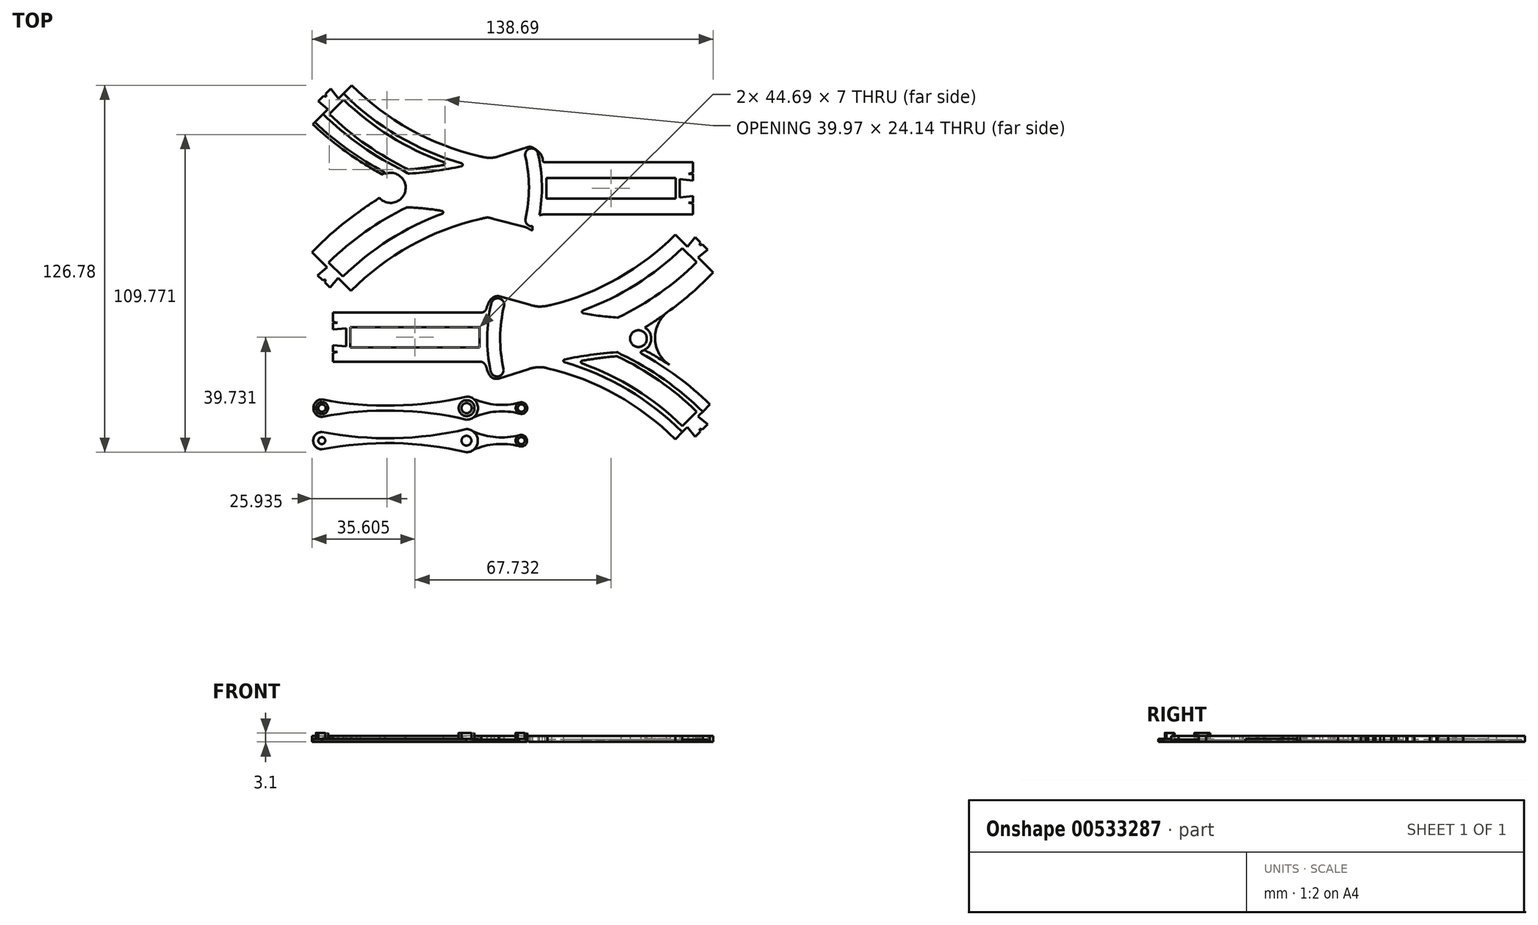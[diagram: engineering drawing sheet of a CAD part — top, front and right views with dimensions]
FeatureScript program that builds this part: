
annotation { "Feature Type Name" : "Feature", "Feature Type Description" : "" }
export const myFeature = defineFeature(function(context is Context, id is Id, definition is map)
    precondition{}
    {
        {
            var Q0;
            Q0=qCreatedBy(makeId("Top.planeOp"),FACE);
            var sketch = newSketch(context, id + "F0", { "sketchPlane" : qUnion([Q0])});
            skLineSegment(sketch, "E0.right", {"start": v(-61.89, -40.1) * mm, "end": v(-61.89, -35.5) * mm});
            skLineSegment(sketch, "E1.bottom", {"start": v(-10.59, -38.6) * mm, "end": v(-61.89, -38.6) * mm});
            skLineSegment(sketch, "E1.right", {"start": v(-61.89, -38.6) * mm, "end": v(-61.89, -40.1) * mm});
            skLineSegment(sketch, "E2.top", {"start": v(-10.59, -21.6) * mm, "end": v(-61.89, -21.6) * mm});
            skLineSegment(sketch, "E2.right", {"start": v(-61.89, -20.1) * mm, "end": v(-61.89, -21.6) * mm});
            skLineSegment(sketch, "E3.top", {"start": v(-10.32, -35.1) * mm, "end": v(-61.89, -35.1) * mm});
            skLineSegment(sketch, "E3.right", {"start": v(-61.89, -38.6) * mm, "end": v(-61.89, -35.5) * mm});
            skLineSegment(sketch, "E4.top", {"start": v(-10.32, -25.1) * mm, "end": v(-61.89, -25.1) * mm});
            skLineSegment(sketch, "E4.right", {"start": v(-61.89, -21.6) * mm, "end": v(-61.89, -24.7) * mm});
            skLineSegment(sketch, "E5", {"start": v(-57.4, -33.26) * mm, "end": v(-61.89, -32.8) * mm});
            skLineSegment(sketch, "E6.MirrorCS", {"start": v(-57.4, -26.96) * mm, "end": v(-61.89, -27.4) * mm});
            skLineSegment(sketch, "E7", {"start": v(-57.4, -33.26) * mm, "end": v(-57.4, -26.96) * mm});
            skLineSegment(sketch, "E8.trimOffspring", {"start": v(-61.89, -24.7) * mm, "end": v(-61.89, -20.1) * mm});
            skLineSegment(sketch, "E9", {"start": v(-61.89, -35.1) * mm, "end": v(-61.89, -32.8) * mm});
            skLineSegment(sketch, "E10", {"start": v(-61.89, -27.4) * mm, "end": v(-61.89, -25.1) * mm});
            skLineSegment(sketch, "E11", {"start": v(-61.89, -35.5) * mm, "end": v(-60.39, -35.1) * mm});
            skLineSegment(sketch, "E12", {"start": v(-61.89, -24.7) * mm, "end": v(-60.39, -25.1) * mm});
            skLineSegment(sketch, "E13.right", {"start": v(-55.9, -33.6) * mm, "end": v(-55.9, -30.1) * mm});
            skArc(sketch, "E14", {"start": v(13.02, -17.5) * mm, "mid": v(35.83, -8.48) * mm, "end": v(55.36, 6.37) * mm});
            skArc(sketch, "E15", {"start": v(13.65, -18.9) * mm, "mid": v(36.7, -9.71) * mm, "end": v(56.42, 5.31) * mm});
            skArc(sketch, "E16", {"start": v(18.9, -21.08) * mm, "mid": v(40.39, -11.61) * mm, "end": v(58.9, 2.84) * mm});
            skArc(sketch, "E17", {"start": v(24.51, -20.8) * mm, "mid": v(42.85, -11.86) * mm, "end": v(58.9, 0.73) * mm});
            skArc(sketch, "E18", {"start": v(37.87, -24.35) * mm, "mid": v(52.76, -15.45) * mm, "end": v(65.98, -4.22) * mm});
            skArc(sketch, "E19", {"start": v(11.95, -42.28) * mm, "mid": v(35.32, -51.31) * mm, "end": v(55.33, -66.4) * mm});
            skArc(sketch, "E20", {"start": v(12.09, -40.78) * mm, "mid": v(35.96, -49.95) * mm, "end": v(56.39, -65.34) * mm});
            skArc(sketch, "E21", {"start": v(18.13, -38.74) * mm, "mid": v(40.02, -48.24) * mm, "end": v(58.86, -62.87) * mm});
            skLineSegment(sketch, "E22", {"start": v(55.36, 6.37) * mm, "end": v(60.58, 1.17) * mm});
            skLineSegment(sketch, "E23", {"start": v(55.33, -66.4) * mm, "end": v(59.92, -61.8) * mm});
            skArc(sketch, "E24.trimOffspring", {"start": v(24.17, -39.14) * mm, "mid": v(42.67, -48.1) * mm, "end": v(58.85, -60.75) * mm});
            skArc(sketch, "E25.trimOffspring", {"start": v(36.3, -36.62) * mm, "mid": v(50.84, -45.1) * mm, "end": v(63.8, -55.8) * mm});
            skArc(sketch, "E26.trimOffspring", {"start": v(37.7, -36) * mm, "mid": v(52.64, -44.73) * mm, "end": v(65.93, -55.8) * mm});
            skArc(sketch, "E27.trimOffspring", {"start": v(44.78, -35.76) * mm, "mid": v(57.2, -43.74) * mm, "end": v(68.4, -53.32) * mm});
            skArc(sketch, "E28.trimOffspring", {"start": v(36.76, -23.23) * mm, "mid": v(51.07, -14.81) * mm, "end": v(63.85, -4.22) * mm});
            skArc(sketch, "E29", {"start": v(54.66, -20.73) * mm, "mid": v(62.38, -14.58) * mm, "end": v(69.52, -7.75) * mm});
            skArc(sketch, "E30", {"start": v(54.4, -39.65) * mm, "mid": v(62.22, -45.62) * mm, "end": v(69.47, -52.26) * mm});
            skArc(sketch, "E31", {"start": v(54.66, -20.73) * mm, "mid": v(49.42, -30.12) * mm, "end": v(54.4, -39.65) * mm});
            skArc(sketch, "E32", {"start": v(-4.25, -15.97) * mm, "mid": v(-5.74, -15.98) * mm, "end": v(-7.04, -16.7) * mm});
            skCircle(sketch, "E33", {"center": v(43.7, -30.57) * mm, "radius": 2.9 * mm});
            skArc(sketch, "E34", {"start": v(-2.75, -19.24) * mm, "mid": v(-4.58, -16.66) * mm, "end": v(-7.18, -18.46) * mm});
            skArc(sketch, "E35.trimOffspring", {"start": v(44.57, -25.78) * mm, "mid": v(57.19, -17.08) * mm, "end": v(68.46, -6.7) * mm});
            skArc(sketch, "E36.trimOffspring", {"start": v(45.91, -26.73) * mm, "mid": v(50.36, -23.84) * mm, "end": v(54.66, -20.73) * mm});
            skArc(sketch, "E37.trimOffspring", {"start": v(45.73, -34.5) * mm, "mid": v(50.13, -36.98) * mm, "end": v(54.4, -39.65) * mm});
            skLineSegment(sketch, "E38", {"start": v(-55.9, -26.6) * mm, "end": v(-11.22, -26.6) * mm});
            skLineSegment(sketch, "E39", {"start": v(-55.9, -33.6) * mm, "end": v(-11.22, -33.6) * mm});
            skArc(sketch, "E40", {"start": v(36.17, -35.27) * mm, "mid": v(27.12, -36.2) * mm, "end": v(18.17, -37.77) * mm});
            skLineSegment(sketch, "E41", {"start": v(18.9, -21.08) * mm, "end": v(18.39, -21.24) * mm});
            skLineSegment(sketch, "E42", {"start": v(37.87, -24.35) * mm, "end": v(37.02, -24.88) * mm});
            skLineSegment(sketch, "E43", {"start": v(12.09, -40.78) * mm, "end": v(11.44, -40.63) * mm});
            skLineSegment(sketch, "E44", {"start": v(37.7, -36) * mm, "end": v(36.76, -35.42) * mm});
            skLineSegment(sketch, "E45", {"start": v(6.23, -18.9) * mm, "end": v(-4.25, -15.97) * mm});
            skFitSpline(sketch, "E46", {"points": [v(-8.82, -20.06) * mm, v(-7.04, -16.7) * mm, v(-4.25, -15.97) * mm], "startDerivative": vector(2.43, 8.58) * mm, "endDerivative": vector(7.45, -1.74) * mm});
            skLineSegment(sketch, "E47", {"start": v(5.76, -41.06) * mm, "end": v(-4.6, -44.37) * mm});
            skFitSpline(sketch, "E48", {"points": [v(-8.98, -40.2) * mm, v(-7.4, -43.67) * mm, v(-4.6, -44.37) * mm], "startDerivative": vector(2.7, -8.06) * mm, "endDerivative": vector(7.78, 1.84) * mm});
            skArc(sketch, "E49", {"start": v(-7.13, -18.25) * mm, "mid": v(-8.6, -30.15) * mm, "end": v(-7.32, -42.07) * mm});
            skArc(sketch, "E50", {"start": v(-2.75, -19.24) * mm, "mid": v(-4.11, -30.11) * mm, "end": v(-2.96, -41.01) * mm});
            skArc(sketch, "E51", {"start": v(-7.4, -41.72) * mm, "mid": v(-4.82, -43.63) * mm, "end": v(-2.96, -41.01) * mm});
            skLineSegment(sketch, "E52", {"start": v(-4.02, -45.87) * mm, "end": v(6.3, -42.46) * mm});
            skLineSegment(sketch, "E53", {"start": v(14.4, -19.56) * mm, "end": v(14.4, -19.56) * mm});
            skFitSpline(sketch, "E54", {"points": [v(-4.02, -45.87) * mm, v(-8.28, -44.88) * mm, v(-10.33, -40.85) * mm], "startDerivative": vector(-10.27, -1.82) * mm, "endDerivative": vector(-1.73, 10.08) * mm});
            skLineSegment(sketch, "E55", {"start": v(6.35, -17.37) * mm, "end": v(-4.44, -14.36) * mm});
            skFitSpline(sketch, "E56", {"points": [v(6.3, -42.46) * mm, v(11.95, -42.28) * mm], "startDerivative": vector(4.48, 1.48) * mm, "endDerivative": vector(4.94, -1) * mm});
            skFitSpline(sketch, "E57", {"points": [v(5.76, -41.06) * mm, v(12.29, -40.82) * mm], "startDerivative": vector(6.34, 1.97) * mm, "endDerivative": vector(7.02, -1.91) * mm});
            skArc(sketch, "E58.trimOffspring", {"start": v(18.42, -22.2) * mm, "mid": v(27.52, -23.9) * mm, "end": v(36.71, -24.95) * mm});
            skFitSpline(sketch, "E59", {"points": [v(-4.44, -14.36) * mm, v(-7.95, -15.52) * mm, v(-10.15, -19.36) * mm], "startDerivative": vector(-8.7, -0.53) * mm, "endDerivative": vector(-3.43, -9.13) * mm});
            skFitSpline(sketch, "E60", {"points": [v(6.35, -17.37) * mm, v(13.02, -17.5) * mm], "startDerivative": vector(8.86, -2.5) * mm, "endDerivative": vector(9.69, 2.19) * mm});
            skFitSpline(sketch, "E61", {"points": [v(6.23, -18.9) * mm, v(13.65, -18.9) * mm], "startDerivative": vector(7.97, -2.48) * mm, "endDerivative": vector(9.92, 2.27) * mm});
            skFitSpline(sketch, "E62", {"points": [v(-14.72, -20.1) * mm, v(-8.7, -16.34) * mm], "startDerivative": vector(9.37, 0) * mm, "endDerivative": vector(3.18, 5.82) * mm});
            skLineSegment(sketch, "E63.trimOffspring", {"start": v(-14.72, -20.1) * mm, "end": v(-61.89, -20.1) * mm});
            skFitSpline(sketch, "E64", {"points": [v(-10.59, -21.6) * mm, v(-8.82, -20.06) * mm], "startDerivative": vector(2.32, 0.32) * mm, "endDerivative": vector(0.74, 2.93) * mm});
            skArc(sketch, "E65.trimOffspring", {"start": v(-9.58, -25.91) * mm, "mid": v(-9.72, -30.1) * mm, "end": v(-9.58, -34.3) * mm});
            skArc(sketch, "E66.filletArc", {"start": v(-9.58, -25.91) * mm, "mid": v(-9.78, -25.35) * mm, "end": v(-10.32, -25.1) * mm});
            skArc(sketch, "E67.filletArc", {"start": v(-10.32, -35.1) * mm, "mid": v(-9.78, -34.87) * mm, "end": v(-9.58, -34.3) * mm});
            skFitSpline(sketch, "E68", {"points": [v(-14.72, -40.1) * mm, v(-9.07, -44.04) * mm], "startDerivative": vector(9.23, 0) * mm, "endDerivative": vector(3.36, -5.87) * mm});
            skLineSegment(sketch, "E69.trimOffspring", {"start": v(-14.72, -40.1) * mm, "end": v(-61.89, -40.1) * mm});
            skFitSpline(sketch, "E70", {"points": [v(-10.59, -38.6) * mm, v(-8.98, -40.2) * mm], "startDerivative": vector(2.4, -0.42) * mm, "endDerivative": vector(0.75, -2.2) * mm});
            skArc(sketch, "E71", {"start": v(44.89, -34.84) * mm, "mid": v(48.13, -30.44) * mm, "end": v(44.64, -26.24) * mm});
            skLineSegment(sketch, "E72", {"start": v(-11.22, -26.6) * mm, "end": v(-11.22, -33.6) * mm});
            skFitSpline(sketch, "E73", {"points": [v(22.86, -21.39) * mm, v(36.65, -23.28) * mm], "startDerivative": vector(10.75, -2.48) * mm, "endDerivative": vector(16.26, -0.75) * mm});
            skArc(sketch, "E74.filletArc", {"start": v(24.51, -20.8) * mm, "mid": v(24.19, -21.31) * mm, "end": v(24.58, -21.76) * mm});
            skArc(sketch, "E75.filletArc", {"start": v(36.52, -23.28) * mm, "mid": v(36.64, -23.27) * mm, "end": v(36.76, -23.23) * mm});
            skFitSpline(sketch, "E76", {"points": [v(22.35, -38.51) * mm, v(36.3, -36.62) * mm], "startDerivative": vector(13.99, 2.55) * mm, "endDerivative": vector(14.95, 1.52) * mm});
            skArc(sketch, "E77.filletArc", {"start": v(24.26, -38.18) * mm, "mid": v(23.84, -38.63) * mm, "end": v(24.17, -39.14) * mm});
            skLineSegment(sketch, "E78", {"start": v(64.85, 1.72) * mm, "end": v(65.81, 1.98) * mm});
            skLineSegment(sketch, "E79", {"start": v(65.81, 1.98) * mm, "end": v(67.6, 0.2) * mm});
            skLineSegment(sketch, "E80", {"start": v(67.6, 0.2) * mm, "end": v(64.3, -2.55) * mm});
            skLineSegment(sketch, "E81.MirrorCS", {"start": v(63.28, 4.5) * mm, "end": v(60.58, 1.17) * mm});
            skLineSegment(sketch, "E82.MirrorCS", {"start": v(65.1, 2.69) * mm, "end": v(63.28, 4.5) * mm});
            skLineSegment(sketch, "E83.MirrorCS", {"start": v(64.85, 1.72) * mm, "end": v(65.1, 2.69) * mm});
            skLineSegment(sketch, "E84", {"start": v(64.84, -61.73) * mm, "end": v(65.1, -62.7) * mm});
            skLineSegment(sketch, "E85", {"start": v(65.1, -62.7) * mm, "end": v(63.3, -64.5) * mm});
            skLineSegment(sketch, "E86", {"start": v(63.3, -64.5) * mm, "end": v(60.59, -61.16) * mm});
            skLineSegment(sketch, "E87.MirrorCS", {"start": v(67.6, -60.18) * mm, "end": v(64.26, -57.48) * mm});
            skLineSegment(sketch, "E88.MirrorCS", {"start": v(65.8, -61.99) * mm, "end": v(67.6, -60.18) * mm});
            skLineSegment(sketch, "E89.MirrorCS", {"start": v(64.84, -61.73) * mm, "end": v(65.8, -61.99) * mm});
            skArc(sketch, "E90.filletArc", {"start": v(18.17, -37.77) * mm, "mid": v(17.77, -38.24) * mm, "end": v(18.13, -38.74) * mm});
            skPoint(sketch, "E91.visualSharp", {"position": v(36.5, -35.25) * mm});
            skArc(sketch, "E91.filletArc", {"start": v(36.76, -35.42) * mm, "mid": v(36.48, -35.3) * mm, "end": v(36.17, -35.27) * mm});
            skPoint(sketch, "E92.visualSharp", {"position": v(43.36, -35) * mm});
            skArc(sketch, "E92.filletArc", {"start": v(44.89, -34.84) * mm, "mid": v(44.53, -35.26) * mm, "end": v(44.78, -35.76) * mm});
            skPoint(sketch, "E93.visualSharp", {"position": v(16.57, -21.78) * mm});
            skArc(sketch, "E93.filletArc", {"start": v(18.39, -21.24) * mm, "mid": v(18.03, -21.74) * mm, "end": v(18.42, -22.2) * mm});
            skPoint(sketch, "E94.visualSharp", {"position": v(36.88, -24.96) * mm});
            skArc(sketch, "E94.filletArc", {"start": v(36.71, -24.95) * mm, "mid": v(36.87, -24.94) * mm, "end": v(37.02, -24.88) * mm});
            skPoint(sketch, "E95.visualSharp", {"position": v(43.95, -26.14) * mm});
            skArc(sketch, "E95.filletArc", {"start": v(44.57, -25.78) * mm, "mid": v(44.45, -26.03) * mm, "end": v(44.64, -26.24) * mm});
            skLineSegment(sketch, "E96", {"start": v(-55.9, -30.1) * mm, "end": v(-55.9, -26.6) * mm});
            skLineSegment(sketch, "E97.trimOffspring", {"start": v(64.3, -2.55) * mm, "end": v(69.52, -7.75) * mm});
            skLineSegment(sketch, "E98.trimOffspring", {"start": v(64.87, -56.86) * mm, "end": v(69.47, -52.26) * mm});
            skLineSegment(sketch, "E99", {"start": v(60.59, -61.16) * mm, "end": v(59.92, -61.8) * mm});
            skLineSegment(sketch, "E100", {"start": v(64.26, -57.48) * mm, "end": v(64.87, -56.86) * mm});
            skLineSegment(sketch, "E101.right", {"start": v(62.49, 31.38) * mm, "end": v(62.49, 26.78) * mm});
            skLineSegment(sketch, "E102.bottom", {"start": v(11.19, 30.38) * mm, "end": v(62.49, 30.38) * mm});
            skLineSegment(sketch, "E102.right", {"start": v(62.49, 30.38) * mm, "end": v(62.49, 31.38) * mm});
            skLineSegment(sketch, "E103.top", {"start": v(11.19, 12.38) * mm, "end": v(62.49, 12.38) * mm});
            skLineSegment(sketch, "E103.right", {"start": v(62.49, 11.38) * mm, "end": v(62.49, 12.38) * mm});
            skLineSegment(sketch, "E104.top", {"start": v(10.92, 26.38) * mm, "end": v(62.49, 26.38) * mm});
            skLineSegment(sketch, "E104.right", {"start": v(62.49, 30.38) * mm, "end": v(62.49, 26.78) * mm});
            skLineSegment(sketch, "E105.top", {"start": v(10.92, 16.38) * mm, "end": v(62.49, 16.38) * mm});
            skLineSegment(sketch, "E105.right", {"start": v(62.49, 12.38) * mm, "end": v(62.49, 15.98) * mm});
            skLineSegment(sketch, "E106", {"start": v(58, 24.53) * mm, "end": v(62.49, 24.08) * mm});
            skLineSegment(sketch, "E107.MirrorCS", {"start": v(58, 18.23) * mm, "end": v(62.49, 18.68) * mm});
            skLineSegment(sketch, "E108", {"start": v(58, 24.53) * mm, "end": v(58, 18.23) * mm});
            skLineSegment(sketch, "E109.trimOffspring", {"start": v(62.49, 15.98) * mm, "end": v(62.49, 11.38) * mm});
            skLineSegment(sketch, "E110", {"start": v(62.49, 26.38) * mm, "end": v(62.49, 24.08) * mm});
            skLineSegment(sketch, "E111", {"start": v(62.49, 18.68) * mm, "end": v(62.49, 16.38) * mm});
            skLineSegment(sketch, "E112", {"start": v(62.49, 26.78) * mm, "end": v(60.99, 26.38) * mm});
            skLineSegment(sketch, "E113", {"start": v(62.49, 15.98) * mm, "end": v(60.99, 16.38) * mm});
            skLineSegment(sketch, "E114.right", {"start": v(56.5, 24.88) * mm, "end": v(56.5, 21.38) * mm});
            skArc(sketch, "E115", {"start": v(-12.42, 9.41) * mm, "mid": v(-35.35, 0.23) * mm, "end": v(-54.94, -14.8) * mm});
            skArc(sketch, "E116", {"start": v(-11.23, 10.72) * mm, "mid": v(-35.2, 1.46) * mm, "end": v(-55.65, -14.1) * mm});
            skArc(sketch, "E117", {"start": v(-18.02, 13.06) * mm, "mid": v(-39.79, 3.43) * mm, "end": v(-58.5, -11.29) * mm});
            skArc(sketch, "E118", {"start": v(-24.13, 12.6) * mm, "mid": v(-42.47, 3.53) * mm, "end": v(-58.5, -9.17) * mm});
            skArc(sketch, "E119", {"start": v(-37.5, 16.08) * mm, "mid": v(-52.4, 7.08) * mm, "end": v(-65.61, -4.25) * mm});
            skArc(sketch, "E120", {"start": v(-11.36, 33.53) * mm, "mid": v(-34.74, 42.56) * mm, "end": v(-54.74, 57.65) * mm});
            skArc(sketch, "E121", {"start": v(-11.38, 32.5) * mm, "mid": v(-35.13, 41.63) * mm, "end": v(-55.45, 56.94) * mm});
            skArc(sketch, "E122", {"start": v(-17.42, 29.95) * mm, "mid": v(-39.38, 39.45) * mm, "end": v(-58.28, 54.11) * mm});
            skLineSegment(sketch, "E123", {"start": v(-54.94, -14.8) * mm, "end": v(-60.18, -9.62) * mm});
            skLineSegment(sketch, "E124", {"start": v(-54.74, 57.65) * mm, "end": v(-59.34, 53.05) * mm});
            skArc(sketch, "E125.trimOffspring", {"start": v(-23.58, 30.4) * mm, "mid": v(-42.08, 39.34) * mm, "end": v(-58.27, 52) * mm});
            skArc(sketch, "E126.trimOffspring", {"start": v(-35.7, 27.86) * mm, "mid": v(-50.25, 36.33) * mm, "end": v(-63.22, 47.05) * mm});
            skArc(sketch, "E127.trimOffspring", {"start": v(-37.13, 27.23) * mm, "mid": v(-52.06, 35.97) * mm, "end": v(-65.35, 47.04) * mm});
            skArc(sketch, "E128.trimOffspring", {"start": v(-44.1, 26.9) * mm, "mid": v(-56.74, 34.73) * mm, "end": v(-68.18, 44.21) * mm});
            skArc(sketch, "E129.trimOffspring", {"start": v(-36.43, 14.75) * mm, "mid": v(-50.72, 6.34) * mm, "end": v(-63.48, -4.25) * mm});
            skArc(sketch, "E130", {"start": v(-53.82, 12.6) * mm, "mid": v(-61.8, 6.28) * mm, "end": v(-69.17, -0.74) * mm});
            skArc(sketch, "E131", {"start": v(-53.57, 31.35) * mm, "mid": v(-61.5, 37.09) * mm, "end": v(-68.89, 43.5) * mm});
            skArc(sketch, "E132", {"start": v(-53.82, 12.6) * mm, "mid": v(-48.6, 21.9) * mm, "end": v(-53.57, 31.35) * mm});
            skArc(sketch, "E133", {"start": v(4.32, 8.02) * mm, "mid": v(5.36, 7.29) * mm, "end": v(6.59, 6.96) * mm});
            skCircle(sketch, "E134", {"center": v(-41.99, 21.52) * mm, "radius": 2.9 * mm});
            skArc(sketch, "E135", {"start": v(4.62, 10.76) * mm, "mid": v(6.6, 8.23) * mm, "end": v(9.1, 10.28) * mm});
            skArc(sketch, "E136.trimOffspring", {"start": v(-44.8, 17.5) * mm, "mid": v(-57.3, 8.86) * mm, "end": v(-68.45, -1.45) * mm});
            skArc(sketch, "E137.trimOffspring", {"start": v(-45.43, 18.29) * mm, "mid": v(-49.7, 15.54) * mm, "end": v(-53.82, 12.6) * mm});
            skArc(sketch, "E138.trimOffspring", {"start": v(-44.63, 26.05) * mm, "mid": v(-49.16, 28.6) * mm, "end": v(-53.57, 31.35) * mm});
            skLineSegment(sketch, "E139", {"start": v(56.5, 17.88) * mm, "end": v(11.82, 17.88) * mm});
            skLineSegment(sketch, "E140", {"start": v(56.5, 24.88) * mm, "end": v(11.82, 24.88) * mm});
            skArc(sketch, "E141", {"start": v(-35.51, 26.46) * mm, "mid": v(-26.44, 27.4) * mm, "end": v(-17.46, 28.98) * mm});
            skLineSegment(sketch, "E142", {"start": v(-18.02, 13.06) * mm, "end": v(-18.02, 13.06) * mm});
            skLineSegment(sketch, "E143", {"start": v(-37.5, 16.08) * mm, "end": v(-36.53, 16.67) * mm});
            skLineSegment(sketch, "E144", {"start": v(-11.58, 32.55) * mm, "end": v(-11.38, 32.5) * mm});
            skLineSegment(sketch, "E145", {"start": v(-37.13, 27.23) * mm, "end": v(-36.12, 26.61) * mm});
            skLineSegment(sketch, "E146", {"start": v(-6.22, 10.72) * mm, "end": v(4.32, 8.02) * mm});
            skFitSpline(sketch, "E147", {"points": [v(6.94, 10.75) * mm, v(7, 6.96) * mm, v(4.32, 8.02) * mm], "startDerivative": vector(-1.82, -6.41) * mm, "endDerivative": vector(-8.94, 2.16) * mm});
            skLineSegment(sketch, "E148", {"start": v(-5.03, 32.29) * mm, "end": v(5.33, 35.59) * mm});
            skFitSpline(sketch, "E149", {"points": [v(10.52, 31.9) * mm, v(8.12, 34.84) * mm, v(5.33, 35.59) * mm], "startDerivative": vector(-2.67, 7.98) * mm, "endDerivative": vector(-7.78, -1.84) * mm});
            skArc(sketch, "E150", {"start": v(8.96, 9.68) * mm, "mid": v(10.31, 21.68) * mm, "end": v(8.88, 33.66) * mm});
            skArc(sketch, "E151", {"start": v(4.62, 10.76) * mm, "mid": v(5.84, 21.7) * mm, "end": v(4.53, 32.64) * mm});
            skArc(sketch, "E152", {"start": v(9, 33.15) * mm, "mid": v(6.51, 35.14) * mm, "end": v(4.53, 32.64) * mm});
            skLineSegment(sketch, "E153", {"start": v(4.6, 36.59) * mm, "end": v(-5.69, 33.04) * mm});
            skLineSegment(sketch, "E154", {"start": v(-34.93, 61.02) * mm, "end": v(-34.93, 61.02) * mm});
            skFitSpline(sketch, "E155", {"points": [v(4.6, 36.59) * mm, v(8.74, 35.62) * mm, v(10.32, 32.88) * mm], "startDerivative": vector(10.25, 1.82) * mm, "endDerivative": vector(0.33, -1.62) * mm});
            skLineSegment(sketch, "E156", {"start": v(-5.26, 8.93) * mm, "end": v(5.6, 6.15) * mm});
            skFitSpline(sketch, "E157", {"points": [v(-5.69, 33.04) * mm, v(-11.36, 33.53) * mm], "startDerivative": vector(-4.48, -1.48) * mm, "endDerivative": vector(-4.94, 1) * mm});
            skFitSpline(sketch, "E158", {"points": [v(-5.03, 32.29) * mm, v(-11.58, 32.56) * mm], "startDerivative": vector(-6.38, -1.98) * mm, "endDerivative": vector(-7.02, 1.91) * mm});
            skArc(sketch, "E159.trimOffspring", {"start": v(-18.06, 14.02) * mm, "mid": v(-27.1, 15.7) * mm, "end": v(-36.23, 16.74) * mm});
            skFitSpline(sketch, "E160", {"points": [v(5.6, 6.15) * mm, v(6.83, 5.46) * mm, v(6.73, 9.27) * mm], "startDerivative": vector(10.04, 0.65) * mm, "endDerivative": vector(4.27, 11.38) * mm});
            skFitSpline(sketch, "E161", {"points": [v(-5.26, 8.93) * mm, v(-12.42, 9.41) * mm], "startDerivative": vector(-8.86, 2.5) * mm, "endDerivative": vector(-9.69, -2.22) * mm});
            skFitSpline(sketch, "E162", {"points": [v(-6.22, 10.72) * mm, v(-11.23, 10.72) * mm], "startDerivative": vector(-7.97, 2.48) * mm, "endDerivative": vector(-9.23, -1.97) * mm});
            skFitSpline(sketch, "E163", {"points": [v(15.32, 11.38) * mm, v(6.46, 6.04) * mm], "startDerivative": vector(-9.37, 0) * mm, "endDerivative": vector(-3.18, -5.82) * mm});
            skLineSegment(sketch, "E164.trimOffspring", {"start": v(15.32, 11.38) * mm, "end": v(62.49, 11.38) * mm});
            skFitSpline(sketch, "E165", {"points": [v(11.19, 12.38) * mm, v(6.94, 10.75) * mm], "startDerivative": vector(-2.32, -0.32) * mm, "endDerivative": vector(-0.74, -2.93) * mm});
            skArc(sketch, "E166.trimOffspring", {"start": v(10.18, 17.18) * mm, "mid": v(10.32, 21.38) * mm, "end": v(10.18, 25.57) * mm});
            skArc(sketch, "E167.filletArc", {"start": v(10.18, 17.18) * mm, "mid": v(10.38, 16.61) * mm, "end": v(10.92, 16.38) * mm});
            skArc(sketch, "E168.filletArc", {"start": v(10.92, 26.38) * mm, "mid": v(10.38, 26.14) * mm, "end": v(10.18, 25.57) * mm});
            skFitSpline(sketch, "E169", {"points": [v(15.32, 31.38) * mm, v(10.14, 33.36) * mm], "startDerivative": vector(-11.97, -1) * mm, "endDerivative": vector(-2.4, 5.7) * mm});
            skLineSegment(sketch, "E170.trimOffspring", {"start": v(15.32, 31.38) * mm, "end": v(62.49, 31.38) * mm});
            skFitSpline(sketch, "E171", {"points": [v(11.19, 30.38) * mm, v(10.52, 31.9) * mm], "startDerivative": vector(-2.4, 0.42) * mm, "endDerivative": vector(-0.75, 2.2) * mm});
            skLineSegment(sketch, "E172", {"start": v(11.82, 17.88) * mm, "end": v(11.82, 24.88) * mm});
            skFitSpline(sketch, "E173", {"points": [v(-22.47, 13.2) * mm, v(-36.32, 14.8) * mm], "startDerivative": vector(-10.84, 2.5) * mm, "endDerivative": vector(-16.25, 0.75) * mm});
            skArc(sketch, "E174.filletArc", {"start": v(-24.13, 12.6) * mm, "mid": v(-23.8, 13.1) * mm, "end": v(-24.21, 13.56) * mm});
            skArc(sketch, "E175.filletArc", {"start": v(-36.2, 14.8) * mm, "mid": v(-36.31, 14.8) * mm, "end": v(-36.43, 14.75) * mm});
            skFitSpline(sketch, "E176", {"points": [v(-21.76, 29.76) * mm, v(-35.7, 27.86) * mm], "startDerivative": vector(-13.99, -2.55) * mm, "endDerivative": vector(-14.95, -1.52) * mm});
            skArc(sketch, "E177.filletArc", {"start": v(-23.66, 29.43) * mm, "mid": v(-23.25, 29.88) * mm, "end": v(-23.58, 30.4) * mm});
            skLineSegment(sketch, "E178", {"start": v(-64.46, -10.19) * mm, "end": v(-65.43, -10.44) * mm});
            skLineSegment(sketch, "E179", {"start": v(-65.43, -10.44) * mm, "end": v(-67.23, -8.68) * mm});
            skLineSegment(sketch, "E180", {"start": v(-67.23, -8.68) * mm, "end": v(-63.93, -5.92) * mm});
            skLineSegment(sketch, "E181.MirrorCS", {"start": v(-62.89, -12.96) * mm, "end": v(-60.18, -9.62) * mm});
            skLineSegment(sketch, "E182.MirrorCS", {"start": v(-64.72, -11.15) * mm, "end": v(-62.89, -12.96) * mm});
            skLineSegment(sketch, "E183.MirrorCS", {"start": v(-64.46, -10.19) * mm, "end": v(-64.72, -11.15) * mm});
            skLineSegment(sketch, "E184", {"start": v(-64.24, 53) * mm, "end": v(-64.5, 53.96) * mm});
            skLineSegment(sketch, "E185", {"start": v(-64.5, 53.96) * mm, "end": v(-62.71, 55.74) * mm});
            skLineSegment(sketch, "E186", {"start": v(-62.71, 55.74) * mm, "end": v(-60, 52.4) * mm});
            skLineSegment(sketch, "E187.MirrorCS", {"start": v(-67.03, 51.43) * mm, "end": v(-63.68, 48.73) * mm});
            skLineSegment(sketch, "E188.MirrorCS", {"start": v(-65.2, 53.25) * mm, "end": v(-67.03, 51.43) * mm});
            skLineSegment(sketch, "E189.MirrorCS", {"start": v(-64.24, 53) * mm, "end": v(-65.2, 53.25) * mm});
            skArc(sketch, "E190.filletArc", {"start": v(-17.46, 28.98) * mm, "mid": v(-17.06, 29.45) * mm, "end": v(-17.42, 29.95) * mm});
            skPoint(sketch, "E191.visualSharp", {"position": v(-35.84, 26.44) * mm});
            skArc(sketch, "E191.filletArc", {"start": v(-36.12, 26.61) * mm, "mid": v(-35.83, 26.49) * mm, "end": v(-35.51, 26.46) * mm});
            skPoint(sketch, "E192.visualSharp", {"position": v(-16.2, 13.6) * mm});
            skArc(sketch, "E192.filletArc", {"start": v(-18.02, 13.06) * mm, "mid": v(-17.66, 13.55) * mm, "end": v(-18.06, 14.02) * mm});
            skPoint(sketch, "E193.visualSharp", {"position": v(-36.4, 16.75) * mm});
            skArc(sketch, "E193.filletArc", {"start": v(-36.23, 16.74) * mm, "mid": v(-36.39, 16.72) * mm, "end": v(-36.53, 16.67) * mm});
            skLineSegment(sketch, "E194", {"start": v(56.5, 21.38) * mm, "end": v(56.5, 17.88) * mm});
            skLineSegment(sketch, "E195.trimOffspring", {"start": v(-63.93, -5.92) * mm, "end": v(-69.17, -0.74) * mm});
            skLineSegment(sketch, "E196.trimOffspring", {"start": v(-64.29, 48.1) * mm, "end": v(-68.89, 43.5) * mm});
            skLineSegment(sketch, "E197", {"start": v(-60, 52.4) * mm, "end": v(-59.34, 53.05) * mm});
            skLineSegment(sketch, "E198", {"start": v(-63.68, 48.73) * mm, "end": v(-64.29, 48.1) * mm});
            skPoint(sketch, "E199", {"position": v(58.9, 0.73) * mm});
            skPoint(sketch, "E200", {"position": v(63.85, -4.22) * mm});
            skLineSegment(sketch, "E201", {"start": v(58.9, 0.73) * mm, "end": v(63.85, -4.22) * mm});
            skPoint(sketch, "E202.orphan", {"position": v(59.96, 1.78) * mm});
            skPoint(sketch, "E203.orphan", {"position": v(64.92, -3.16) * mm});
            skPoint(sketch, "E204", {"position": v(58.85, -60.75) * mm});
            skPoint(sketch, "E205", {"position": v(63.8, -55.8) * mm});
            skLineSegment(sketch, "E206", {"start": v(58.85, -60.75) * mm, "end": v(63.8, -55.8) * mm});
            skPoint(sketch, "E207", {"position": v(-63.48, -4.25) * mm});
            skPoint(sketch, "E208", {"position": v(-58.5, -9.17) * mm});
            skLineSegment(sketch, "E209", {"start": v(-63.48, -4.25) * mm, "end": v(-58.5, -9.17) * mm});
            skPoint(sketch, "E210.orphan", {"position": v(-64.55, -5.3) * mm});
            skPoint(sketch, "E211.orphan", {"position": v(-59.56, -10.23) * mm});
            skPoint(sketch, "E212", {"position": v(-63.22, 47.05) * mm});
            skPoint(sketch, "E213", {"position": v(-58.27, 52) * mm});
            skLineSegment(sketch, "E214", {"start": v(-63.22, 47.05) * mm, "end": v(-58.27, 52) * mm});
            skPoint(sketch, "E215", {"position": v(-48.5, 29.35) * mm});
            skPoint(sketch, "E216", {"position": v(-48.89, 28.43) * mm});
            skPoint(sketch, "E217", {"position": v(-46.53, 32.35) * mm});
            skLineSegment(sketch, "E218", {"start": v(-44.1, 26.9) * mm, "end": v(-44.63, 26.05) * mm});
            skArc(sketch, "E219", {"start": v(-44.63, 26.05) * mm, "mid": v(-43.97, 26.23) * mm, "end": v(-44.1, 26.9) * mm});
            skArc(sketch, "E220", {"start": v(-44.8, 17.5) * mm, "mid": v(-44.84, 18.12) * mm, "end": v(-45.43, 18.29) * mm});
            skCircle(sketch, "E221", {"center": v(-41.99, 21.52) * mm, "radius": 5.2 * mm});
            skSolve(sketch);
        }
        {
            var Q0;
            Q0=qCreatedBy(makeId("Top.planeOp"),FACE);
            var sketch = newSketch(context, id + "F1", { "sketchPlane" : qUnion([Q0])});
            skArc(sketch, "E222", {"start": v(-65.71, -51.59) * mm, "mid": v(-68.71, -54.59) * mm, "end": v(-65.71, -57.59) * mm});
            skLineSegment(sketch, "E223", {"start": v(-15.77, -54.59) * mm, "end": v(-15.71, -54.59) * mm});
            skArc(sketch, "E224", {"start": v(-15.71, -58.59) * mm, "mid": v(-11.77, -54.59) * mm, "end": v(-15.71, -50.59) * mm});
            skArc(sketch, "E225", {"start": v(-65.71, -51.59) * mm, "mid": v(-40.66, -53.72) * mm, "end": v(-15.71, -50.59) * mm});
            skArc(sketch, "E226", {"start": v(-15.71, -58.59) * mm, "mid": v(-40.66, -55.45) * mm, "end": v(-65.71, -57.59) * mm});
            skCircle(sketch, "E227", {"center": v(-15.71, -54.59) * mm, "radius": 2.75 * mm});
            skCircle(sketch, "E228", {"center": v(-65.71, -54.59) * mm, "radius": 2.1 * mm});
            skPoint(sketch, "E229.endSnap0", {"position": v(-11.77, -54.59) * mm});
            skCircle(sketch, "E230", {"center": v(3.23, -54.59) * mm, "radius": 2 * mm});
            skArc(sketch, "E231", {"start": v(-13.25, -51.47) * mm, "mid": v(-5.5, -53.38) * mm, "end": v(2.48, -52.73) * mm});
            skArc(sketch, "E232.MirrorCS", {"start": v(-13.25, -57.7) * mm, "mid": v(-5.5, -55.8) * mm, "end": v(2.48, -56.44) * mm});
            skCircle(sketch, "E233", {"center": v(-65.71, -54.59) * mm, "radius": 1.25 * mm});
            skCircle(sketch, "E234", {"center": v(-15.71, -54.59) * mm, "radius": 1.75 * mm});
            skCircle(sketch, "E235", {"center": v(3.23, -54.59) * mm, "radius": 1.25 * mm});
            skArc(sketch, "E236", {"start": v(-65.77, -62.84) * mm, "mid": v(-68.77, -65.84) * mm, "end": v(-65.77, -68.84) * mm});
            skArc(sketch, "E237", {"start": v(-15.77, -69.84) * mm, "mid": v(-11.82, -65.84) * mm, "end": v(-15.77, -61.84) * mm});
            skArc(sketch, "E238", {"start": v(-65.77, -62.84) * mm, "mid": v(-40.72, -64.98) * mm, "end": v(-15.77, -61.84) * mm});
            skArc(sketch, "E239", {"start": v(-15.77, -69.84) * mm, "mid": v(-40.72, -66.7) * mm, "end": v(-65.77, -68.84) * mm});
            skPoint(sketch, "E240.endSnap0", {"position": v(-11.82, -65.84) * mm});
            skCircle(sketch, "E241", {"center": v(3.18, -65.84) * mm, "radius": 2 * mm});
            skArc(sketch, "E242", {"start": v(-13.3, -62.73) * mm, "mid": v(-5.55, -64.63) * mm, "end": v(2.42, -64) * mm});
            skArc(sketch, "E243.MirrorCS", {"start": v(-13.3, -68.96) * mm, "mid": v(-5.55, -67.05) * mm, "end": v(2.42, -67.7) * mm});
            skCircle(sketch, "E244", {"center": v(-65.77, -65.84) * mm, "radius": 1.2 * mm});
            skCircle(sketch, "E245", {"center": v(-15.77, -65.84) * mm, "radius": 1.7 * mm});
            skCircle(sketch, "E246", {"center": v(3.18, -65.84) * mm, "radius": 1.2 * mm});
            skLineSegment(sketch, "E247.trimOffspring", {"start": v(-15.82, -65.84) * mm, "end": v(-15.77, -65.84) * mm});
            skSolve(sketch);
        }
        {
            var Q0;
            {var subQ10=sQuery(id+"F0.wireOp",EDGE,"E2.top");Q0=makeQuery(id+"F0.imprint","IMPRINT",FACE,{"disambiguationData":[TD([[makeQuery(id+"F0.imprint","IMPRINT",EDGE,{"derivedFrom":subQ10}),-1.0]])]});}
            var Q1;
            {var subQ3=sQuery(id+"F0.wireOp",EDGE,"E16");Q1=makeQuery(id+"F0.imprint","IMPRINT",FACE,{"disambiguationData":[TD([[makeQuery(id+"F0.imprint","IMPRINT",EDGE,{"derivedFrom":subQ3}),-1.0]])]});}
            var Q2;
            Q2=makeQuery(id+"F0.imprint","IMPRINT",FACE,{"disambiguationData":[TD([[makeQuery(id+"F0.imprint","IMPRINT",EDGE,{"derivedFrom":sQuery(id+"F0.wireOp",EDGE,"E5")}),1.0]])]});
            var Q3;
            {var subQ2=sQuery(id+"F0.wireOp",EDGE,"E21");Q3=makeQuery(id+"F0.imprint","IMPRINT",FACE,{"disambiguationData":[TD([[makeQuery(id+"F0.imprint","IMPRINT",EDGE,{"derivedFrom":subQ2}),1.0]])]});}
            var Q4;
            {var subQ2=sQuery(id+"F0.wireOp",EDGE,"E27.trimOffspring");Q4=makeQuery(id+"F0.imprint","IMPRINT",FACE,{"disambiguationData":[TD([[makeQuery(id+"F0.imprint","IMPRINT",EDGE,{"derivedFrom":subQ2}),1.0]])]});}
            var Q5;
            {var subQ1=sQuery(id+"F0.wireOp",EDGE,"E29");Q5=makeQuery(id+"F0.imprint","IMPRINT",FACE,{"disambiguationData":[TD([[makeQuery(id+"F0.imprint","IMPRINT",EDGE,{"derivedFrom":subQ1}),1.0]])]});}
            var Q6;
            Q6=makeQuery(id+"F0.imprint","IMPRINT",FACE,{"disambiguationData":[TD([[makeQuery(id+"F0.imprint","IMPRINT",EDGE,{"derivedFrom":sQuery(id+"F0.wireOp",EDGE,"E1.right")}),1.0]])]});
            var Q7;
            {var subQ4=sQuery(id+"F0.wireOp",EDGE,"E128.trimOffspring");Q7=makeQuery(id+"F0.imprint","IMPRINT",FACE,{"disambiguationData":[TD([[makeQuery(id+"F0.imprint","IMPRINT",EDGE,{"derivedFrom":subQ4}),1.0]])]});}
            var Q8;
            {var subQ3=sQuery(id+"F0.wireOp",EDGE,"E122");Q8=makeQuery(id+"F0.imprint","IMPRINT",FACE,{"disambiguationData":[TD([[makeQuery(id+"F0.imprint","IMPRINT",EDGE,{"derivedFrom":subQ3}),1.0]])]});}
            var Q9;
            Q9=makeQuery(id+"F0.imprint","IMPRINT",FACE,{"disambiguationData":[TD([[makeQuery(id+"F0.imprint","IMPRINT",EDGE,{"derivedFrom":sQuery(id+"F0.wireOp",EDGE,"E102.right")}),1.0]])]});
            var Q10;
            {var subQ0=sQuery(id+"F0.wireOp",EDGE,"E117");Q10=makeQuery(id+"F0.imprint","IMPRINT",FACE,{"disambiguationData":[TD([[makeQuery(id+"F0.imprint","IMPRINT",EDGE,{"derivedFrom":subQ0}),-1.0]])]});}
            var Q11;
            {var subQ5=sQuery(id+"F0.wireOp",EDGE,"E130");Q11=makeQuery(id+"F0.imprint","IMPRINT",FACE,{"disambiguationData":[TD([[makeQuery(id+"F0.imprint","IMPRINT",EDGE,{"derivedFrom":subQ5}),1.0]])]});}
            var Q12;
            {var subQ10=sQuery(id+"F0.wireOp",EDGE,"E103.top");Q12=makeQuery(id+"F0.imprint","IMPRINT",FACE,{"disambiguationData":[TD([[makeQuery(id+"F0.imprint","IMPRINT",EDGE,{"derivedFrom":subQ10}),-1.0]])]});}
            var Q13;
            Q13=makeQuery(id+"F0.imprint","IMPRINT",FACE,{"disambiguationData":[TD([[makeQuery(id+"F0.imprint","IMPRINT",EDGE,{"derivedFrom":sQuery(id+"F0.wireOp",EDGE,"E106")}),1.0]])]});
            extrude(context, id + "F2", {"entities" : qUnion([Q0, Q1, Q2, Q3, Q4, Q5, Q6, Q7, Q8, Q9, Q10, Q11, Q12, Q13]), "depth" : 2.1 * mm, "offsetDistance" : 25 * mm});
        }
        {
            var Q0;
            Q0=makeQuery(id+"F0.imprint","IMPRINT",FACE,{"disambiguationData":[TD([[makeQuery(id+"F0.imprint","IMPRINT",EDGE,{"derivedFrom":sQuery(id+"F0.wireOp",EDGE,"E1.bottom")}),-1.0]])]});
            var Q1;
            {var subQ2=sQuery(id+"F0.wireOp",EDGE,"E17");Q1=makeQuery(id+"F0.imprint","IMPRINT",FACE,{"disambiguationData":[TD([[makeQuery(id+"F0.imprint","IMPRINT",EDGE,{"derivedFrom":subQ2}),-1.0]])]});}
            var Q2;
            {var subQ0=sQuery(id+"F0.wireOp",EDGE,"E24.trimOffspring");Q2=makeQuery(id+"F0.imprint","IMPRINT",FACE,{"disambiguationData":[TD([[makeQuery(id+"F0.imprint","IMPRINT",EDGE,{"derivedFrom":subQ0}),1.0]])]});}
            var Q3;
            Q3=makeQuery(id+"F0.imprint","IMPRINT",FACE,{"disambiguationData":[TD([[makeQuery(id+"F0.imprint","IMPRINT",EDGE,{"derivedFrom":sQuery(id+"F0.wireOp",EDGE,"E13.right")}),-1.0]])]});
            var Q4;
            Q4=makeQuery(id+"F0.imprint","IMPRINT",FACE,{"disambiguationData":[TD([[makeQuery(id+"F0.imprint","IMPRINT",EDGE,{"derivedFrom":sQuery(id+"F0.wireOp",EDGE,"E102.bottom")}),-1.0]])]});
            var Q5;
            Q5=makeQuery(id+"F0.imprint","IMPRINT",FACE,{"disambiguationData":[TD([[makeQuery(id+"F0.imprint","IMPRINT",EDGE,{"derivedFrom":sQuery(id+"F0.wireOp",EDGE,"E125.trimOffspring")}),1.0]])]});
            var Q6;
            Q6=makeQuery(id+"F0.imprint","IMPRINT",FACE,{"disambiguationData":[TD([[makeQuery(id+"F0.imprint","IMPRINT",EDGE,{"derivedFrom":sQuery(id+"F0.wireOp",EDGE,"E118")}),-1.0]])]});
            var Q7;
            Q7=makeQuery(id+"F0.imprint","IMPRINT",FACE,{"disambiguationData":[TD([[makeQuery(id+"F0.imprint","IMPRINT",EDGE,{"derivedFrom":sQuery(id+"F0.wireOp",EDGE,"E114.right")}),-1.0]])]});
            extrude(context, id + "F3", {"entities" : qUnion([Q0, Q1, Q2, Q3, Q4, Q5, Q6, Q7]), "depth" : 0.8 * mm, "offsetDistance" : 25 * mm});
        }
        {
            var Q0;
            {var subQ0=sQuery(id+"F0.wireOp",EDGE,"E36.trimOffspring");var subQ1=sQuery(id+"F0.wireOp",EDGE,"E31");var subQ2=makeQuery(id+"F0.imprint","INTERSECT",VERTEX,{"derivedFrom":[subQ1,subQ0]});Q0=makeQuery(id+"F0.imprint","IMPRINT",FACE,{"disambiguationData":[TD([[makeQuery(id+"F0.imprint","IMPRINT",EDGE,{"disambiguationData":[TD([[subQ2,-1.0]])],"derivedFrom":subQ1}),-1.0]])]});}
            var Q1;
            {var subQ0=sQuery(id+"F0.wireOp",EDGE,"E138.trimOffspring");Q1=makeQuery(id+"F0.imprint","IMPRINT",FACE,{"disambiguationData":[TD([[makeQuery(id+"F0.imprint","IMPRINT",EDGE,{"derivedFrom":subQ0}),1.0]])]});}
            extrude(context, id + "F4", {"entities" : qUnion([Q0, Q1]), "depth" : 1 * mm, "offsetDistance" : 25 * mm});
        }
        {
            var Q0;
            {var subQ1=sQuery(id+"F1.wireOp",EDGE,"E238");Q0=makeQuery(id+"F1.imprint","IMPRINT",FACE,{"disambiguationData":[TD([[makeQuery(id+"F1.imprint","IMPRINT",EDGE,{"derivedFrom":subQ1}),-1.0]])]});}
            var Q1;
            {var subQ1=sQuery(id+"F1.wireOp",EDGE,"E239");Q1=makeQuery(id+"F1.imprint","IMPRINT",FACE,{"disambiguationData":[TD([[makeQuery(id+"F1.imprint","IMPRINT",EDGE,{"derivedFrom":subQ1}),-1.0]])]});}
            var Q2;
            {var subQ0=sQuery(id+"F1.wireOp",EDGE,"E236");Q2=makeQuery(id+"F1.imprint","IMPRINT",FACE,{"disambiguationData":[TD([[makeQuery(id+"F1.imprint","IMPRINT",EDGE,{"derivedFrom":subQ0}),1.0]])]});}
            var Q3;
            {var subQ0=sQuery(id+"F1.wireOp",EDGE,"E244");var subQ1=sQuery(id+"F1.wireOp",EDGE,"53d5dcf0-674b-4c79-9443-bd6d82ffb135");var subQ2=makeQuery(id+"F1.imprint","INTERSECT",VERTEX,{"derivedFrom":[subQ1,subQ0]});Q3=makeQuery(id+"F1.imprint","IMPRINT",FACE,{"disambiguationData":[TD([[makeQuery(id+"F1.imprint","IMPRINT",EDGE,{"disambiguationData":[TD([[subQ2,-1.0]])],"derivedFrom":subQ1}),1.0]])]});}
            var Q4;
            {var subQ0=sQuery(id+"F1.wireOp",EDGE,"E244");var subQ1=sQuery(id+"F1.wireOp",EDGE,"428ab077-734c-40e8-b26b-1190416dde84");var subQ2=makeQuery(id+"F1.imprint","INTERSECT",VERTEX,{"derivedFrom":[subQ1,subQ0]});Q4=makeQuery(id+"F1.imprint","IMPRINT",FACE,{"disambiguationData":[TD([[makeQuery(id+"F1.imprint","IMPRINT",EDGE,{"disambiguationData":[TD([[subQ2,-1.0]])],"derivedFrom":subQ1}),-1.0]])]});}
            var Q5;
            {var subQ0=sQuery(id+"F1.wireOp",EDGE,"E244");var subQ1=sQuery(id+"F1.wireOp",EDGE,"428ab077-734c-40e8-b26b-1190416dde84");var subQ2=makeQuery(id+"F1.imprint","INTERSECT",VERTEX,{"derivedFrom":[subQ1,subQ0]});Q5=makeQuery(id+"F1.imprint","IMPRINT",FACE,{"disambiguationData":[TD([[makeQuery(id+"F1.imprint","IMPRINT",EDGE,{"disambiguationData":[TD([[subQ2,-1.0]])],"derivedFrom":subQ1}),1.0]])]});}
            var Q6;
            {var subQ0=sQuery(id+"F1.wireOp",EDGE,"E237");var subQ3=makeQuery(id+"F1.imprint","INTERSECT",VERTEX,{"derivedFrom":[subQ0,sQuery(id+"F1.wireOp",EDGE,"E242")]});Q6=makeQuery(id+"F1.imprint","IMPRINT",FACE,{"disambiguationData":[TD([[makeQuery(id+"F1.imprint","IMPRINT",EDGE,{"disambiguationData":[TD([[subQ3,1.0]])],"derivedFrom":subQ0}),1.0]])]});}
            var Q7;
            {var subQ0=sQuery(id+"F1.wireOp",EDGE,"E237");var subQ1=makeQuery(id+"F1.imprint","INTERSECT",VERTEX,{"derivedFrom":[subQ0,sQuery(id+"F1.wireOp",EDGE,"E243.MirrorCS")]});Q7=makeQuery(id+"F1.imprint","IMPRINT",FACE,{"disambiguationData":[TD([[makeQuery(id+"F1.imprint","IMPRINT",EDGE,{"disambiguationData":[TD([[subQ1,-1.0]])],"derivedFrom":subQ0}),1.0]])]});}
            var Q8;
            {var subQ0=sQuery(id+"F1.wireOp",EDGE,"E245");var subQ1=sQuery(id+"F1.wireOp",EDGE,"bc46082b-a8de-4a31-b2da-f92bdda07d0f");var subQ2=makeQuery(id+"F1.imprint","INTERSECT",VERTEX,{"derivedFrom":[subQ1,subQ0]});Q8=makeQuery(id+"F1.imprint","IMPRINT",FACE,{"disambiguationData":[TD([[makeQuery(id+"F1.imprint","IMPRINT",EDGE,{"disambiguationData":[TD([[subQ2,-1.0]])],"derivedFrom":subQ1}),1.0]])]});}
            var Q9;
            {var subQ0=sQuery(id+"F1.wireOp",EDGE,"ea363bf8-e310-4676-b829-d7b3e121218c");var subQ1=sQuery(id+"F1.wireOp",EDGE,"428ab077-734c-40e8-b26b-1190416dde84");var subQ2=makeQuery(id+"F1.imprint","INTERSECT",VERTEX,{"derivedFrom":[subQ1,subQ0]});Q9=makeQuery(id+"F1.imprint","IMPRINT",FACE,{"disambiguationData":[TD([[makeQuery(id+"F1.imprint","IMPRINT",EDGE,{"disambiguationData":[TD([[subQ2,-1.0]])],"derivedFrom":subQ1}),-1.0]])]});}
            var Q10;
            {var subQ0=sQuery(id+"F1.wireOp",EDGE,"E245");var subQ1=sQuery(id+"F1.wireOp",EDGE,"13bed4bd-fcb1-4a5b-8c34-b9fa7a4d6081");var subQ2=makeQuery(id+"F1.imprint","INTERSECT",VERTEX,{"derivedFrom":[subQ1,subQ0]});Q10=makeQuery(id+"F1.imprint","IMPRINT",FACE,{"disambiguationData":[TD([[makeQuery(id+"F1.imprint","IMPRINT",EDGE,{"disambiguationData":[TD([[subQ2,-1.0]])],"derivedFrom":subQ1}),1.0]])]});}
            var Q11;
            {var subQ0=sQuery(id+"F1.wireOp",EDGE,"E245");var subQ1=sQuery(id+"F1.wireOp",EDGE,"13bed4bd-fcb1-4a5b-8c34-b9fa7a4d6081");var subQ2=makeQuery(id+"F1.imprint","INTERSECT",VERTEX,{"derivedFrom":[subQ1,subQ0]});Q11=makeQuery(id+"F1.imprint","IMPRINT",FACE,{"disambiguationData":[TD([[makeQuery(id+"F1.imprint","IMPRINT",EDGE,{"disambiguationData":[TD([[subQ2,-1.0]])],"derivedFrom":subQ1}),-1.0]])]});}
            var Q12;
            Q12=makeQuery(id+"F1.imprint","IMPRINT",FACE,{"disambiguationData":[TD([[makeQuery(id+"F1.imprint","IMPRINT",EDGE,{"derivedFrom":sQuery(id+"F1.wireOp",EDGE,"E246")}),-1.0]])]});
            var Q13;
            {var subQ1=sQuery(id+"F1.wireOp",EDGE,"E223");var subQ3=sQuery(id+"F1.wireOp",EDGE,"E233");var subQ4=makeQuery(id+"F1.imprint","INTERSECT",VERTEX,{"derivedFrom":[subQ1,subQ3]});Q13=makeQuery(id+"F1.imprint","IMPRINT",FACE,{"disambiguationData":[TD([[makeQuery(id+"F1.imprint","IMPRINT",EDGE,{"disambiguationData":[TD([[subQ4,-1.0]])],"derivedFrom":subQ3}),1.0]])]});}
            var Q14;
            {var subQ1=sQuery(id+"F1.wireOp",EDGE,"bf801d30-df9f-42a8-935a-fb90625cb06c");var subQ3=sQuery(id+"F1.wireOp",EDGE,"E233");var subQ4=makeQuery(id+"F1.imprint","INTERSECT",VERTEX,{"derivedFrom":[subQ1,subQ3]});Q14=makeQuery(id+"F1.imprint","IMPRINT",FACE,{"disambiguationData":[TD([[makeQuery(id+"F1.imprint","IMPRINT",EDGE,{"disambiguationData":[TD([[subQ4,-1.0]])],"derivedFrom":subQ3}),1.0]])]});}
            var Q15;
            {var subQ1=sQuery(id+"F1.wireOp",EDGE,"E223");var subQ3=sQuery(id+"F1.wireOp",EDGE,"E233");var subQ4=makeQuery(id+"F1.imprint","INTERSECT",VERTEX,{"derivedFrom":[subQ1,subQ3]});Q15=makeQuery(id+"F1.imprint","IMPRINT",FACE,{"disambiguationData":[TD([[makeQuery(id+"F1.imprint","IMPRINT",EDGE,{"disambiguationData":[TD([[subQ4,1.0]])],"derivedFrom":subQ3}),1.0]])]});}
            var Q16;
            {var subQ1=sQuery(id+"F1.wireOp",EDGE,"E225");Q16=makeQuery(id+"F1.imprint","IMPRINT",FACE,{"disambiguationData":[TD([[makeQuery(id+"F1.imprint","IMPRINT",EDGE,{"derivedFrom":subQ1}),-1.0]])]});}
            var Q17;
            {var subQ1=sQuery(id+"F1.wireOp",EDGE,"E226");Q17=makeQuery(id+"F1.imprint","IMPRINT",FACE,{"disambiguationData":[TD([[makeQuery(id+"F1.imprint","IMPRINT",EDGE,{"derivedFrom":subQ1}),-1.0]])]});}
            var Q18;
            {var subQ0=sQuery(id+"F1.wireOp",EDGE,"E222");Q18=makeQuery(id+"F1.imprint","IMPRINT",FACE,{"disambiguationData":[TD([[makeQuery(id+"F1.imprint","IMPRINT",EDGE,{"derivedFrom":subQ0}),1.0]])]});}
            var Q19;
            {var subQ1=sQuery(id+"F1.wireOp",EDGE,"3a61cfe4-ae7e-431c-9541-1621a5e99a6d");var subQ3=sQuery(id+"F1.wireOp",EDGE,"E234");var subQ4=makeQuery(id+"F1.imprint","INTERSECT",VERTEX,{"derivedFrom":[subQ1,subQ3]});Q19=makeQuery(id+"F1.imprint","IMPRINT",FACE,{"disambiguationData":[TD([[makeQuery(id+"F1.imprint","IMPRINT",EDGE,{"disambiguationData":[TD([[subQ4,1.0]])],"derivedFrom":subQ3}),1.0]])]});}
            var Q20;
            {var subQ1=sQuery(id+"F1.wireOp",EDGE,"3a61cfe4-ae7e-431c-9541-1621a5e99a6d");var subQ3=sQuery(id+"F1.wireOp",EDGE,"E234");var subQ4=makeQuery(id+"F1.imprint","INTERSECT",VERTEX,{"derivedFrom":[subQ1,subQ3]});Q20=makeQuery(id+"F1.imprint","IMPRINT",FACE,{"disambiguationData":[TD([[makeQuery(id+"F1.imprint","IMPRINT",EDGE,{"disambiguationData":[TD([[subQ4,-1.0]])],"derivedFrom":subQ3}),1.0]])]});}
            var Q21;
            {var subQ1=sQuery(id+"F1.wireOp",EDGE,"E223");var subQ3=sQuery(id+"F1.wireOp",EDGE,"E234");var subQ4=makeQuery(id+"F1.imprint","INTERSECT",VERTEX,{"derivedFrom":[subQ1,subQ3]});Q21=makeQuery(id+"F1.imprint","IMPRINT",FACE,{"disambiguationData":[TD([[makeQuery(id+"F1.imprint","IMPRINT",EDGE,{"disambiguationData":[TD([[subQ4,-1.0]])],"derivedFrom":subQ3}),1.0]])]});}
            var Q22;
            {var subQ1=sQuery(id+"F1.wireOp",EDGE,"435c0a83-62e8-43be-807a-781dea070604");var subQ3=sQuery(id+"F1.wireOp",EDGE,"E234");var subQ4=makeQuery(id+"F1.imprint","INTERSECT",VERTEX,{"derivedFrom":[subQ1,subQ3]});Q22=makeQuery(id+"F1.imprint","IMPRINT",FACE,{"disambiguationData":[TD([[makeQuery(id+"F1.imprint","IMPRINT",EDGE,{"disambiguationData":[TD([[subQ4,-1.0]])],"derivedFrom":subQ3}),1.0]])]});}
            var Q23;
            {var subQ0=sQuery(id+"F1.wireOp",EDGE,"E224");var subQ3=makeQuery(id+"F1.imprint","INTERSECT",VERTEX,{"derivedFrom":[subQ0,sQuery(id+"F1.wireOp",EDGE,"E231")]});Q23=makeQuery(id+"F1.imprint","IMPRINT",FACE,{"disambiguationData":[TD([[makeQuery(id+"F1.imprint","IMPRINT",EDGE,{"disambiguationData":[TD([[subQ3,1.0]])],"derivedFrom":subQ0}),1.0]])]});}
            var Q24;
            {var subQ0=sQuery(id+"F1.wireOp",EDGE,"E224");var subQ1=makeQuery(id+"F1.imprint","INTERSECT",VERTEX,{"derivedFrom":[subQ0,sQuery(id+"F1.wireOp",EDGE,"E232.MirrorCS")]});Q24=makeQuery(id+"F1.imprint","IMPRINT",FACE,{"disambiguationData":[TD([[makeQuery(id+"F1.imprint","IMPRINT",EDGE,{"disambiguationData":[TD([[subQ1,-1.0]])],"derivedFrom":subQ0}),1.0]])]});}
            var Q25;
            Q25=makeQuery(id+"F1.imprint","IMPRINT",FACE,{"disambiguationData":[TD([[makeQuery(id+"F1.imprint","IMPRINT",EDGE,{"derivedFrom":sQuery(id+"F1.wireOp",EDGE,"E235")}),1.0]])]});
            var Q26;
            Q26=makeQuery(id+"F1.imprint","IMPRINT",FACE,{"disambiguationData":[TD([[makeQuery(id+"F1.imprint","IMPRINT",EDGE,{"derivedFrom":sQuery(id+"F1.wireOp",EDGE,"E233")}),1.0]])]});
            var Q27;
            Q27=makeQuery(id+"F1.imprint","IMPRINT",FACE,{"disambiguationData":[TD([[makeQuery(id+"F1.imprint","IMPRINT",EDGE,{"derivedFrom":sQuery(id+"F1.wireOp",EDGE,"E234")}),1.0]])]});
            extrude(context, id + "F5", {"entities" : qUnion([Q0, Q1, Q2, Q3, Q4, Q5, Q6, Q7, Q8, Q9, Q10, Q11, Q12, Q13, Q14, Q15, Q16, Q17, Q18, Q19, Q20, Q21, Q22, Q23, Q24, Q25, Q26, Q27]), "depth" : 1.1 * mm, "offsetDistance" : 25 * mm});
        }
        {
            var Q0;
            {var subQ0=sQuery(id+"F1.wireOp",EDGE,"E233");var subQ1=sQuery(id+"F1.wireOp",EDGE,"E223");var subQ2=makeQuery(id+"F1.imprint","INTERSECT",VERTEX,{"derivedFrom":[subQ1,subQ0]});Q0=makeQuery(id+"F1.imprint","IMPRINT",FACE,{"disambiguationData":[TD([[makeQuery(id+"F1.imprint","IMPRINT",EDGE,{"disambiguationData":[TD([[subQ2,-1.0]])],"derivedFrom":subQ1}),1.0]])]});}
            var Q1;
            {var subQ0=sQuery(id+"F1.wireOp",EDGE,"E233");var subQ1=sQuery(id+"F1.wireOp",EDGE,"bf801d30-df9f-42a8-935a-fb90625cb06c");var subQ2=makeQuery(id+"F1.imprint","INTERSECT",VERTEX,{"derivedFrom":[subQ1,subQ0]});Q1=makeQuery(id+"F1.imprint","IMPRINT",FACE,{"disambiguationData":[TD([[makeQuery(id+"F1.imprint","IMPRINT",EDGE,{"disambiguationData":[TD([[subQ2,-1.0]])],"derivedFrom":subQ1}),1.0]])]});}
            var Q2;
            {var subQ0=sQuery(id+"F1.wireOp",EDGE,"E233");var subQ1=sQuery(id+"F1.wireOp",EDGE,"E223");var subQ2=makeQuery(id+"F1.imprint","INTERSECT",VERTEX,{"derivedFrom":[subQ1,subQ0]});Q2=makeQuery(id+"F1.imprint","IMPRINT",FACE,{"disambiguationData":[TD([[makeQuery(id+"F1.imprint","IMPRINT",EDGE,{"disambiguationData":[TD([[subQ2,-1.0]])],"derivedFrom":subQ1}),-1.0]])]});}
            var Q3;
            {var subQ0=sQuery(id+"F1.wireOp",EDGE,"E227");var subQ1=sQuery(id+"F1.wireOp",EDGE,"E223");var subQ2=makeQuery(id+"F1.imprint","INTERSECT",VERTEX,{"derivedFrom":[subQ1,subQ0]});Q3=makeQuery(id+"F1.imprint","IMPRINT",FACE,{"disambiguationData":[TD([[makeQuery(id+"F1.imprint","IMPRINT",EDGE,{"disambiguationData":[TD([[subQ2,-1.0]])],"derivedFrom":subQ1}),-1.0]])]});}
            var Q4;
            {var subQ0=sQuery(id+"F1.wireOp",EDGE,"E234");var subQ1=sQuery(id+"F1.wireOp",EDGE,"3a61cfe4-ae7e-431c-9541-1621a5e99a6d");var subQ2=makeQuery(id+"F1.imprint","INTERSECT",VERTEX,{"derivedFrom":[subQ1,subQ0]});Q4=makeQuery(id+"F1.imprint","IMPRINT",FACE,{"disambiguationData":[TD([[makeQuery(id+"F1.imprint","IMPRINT",EDGE,{"disambiguationData":[TD([[subQ2,-1.0]])],"derivedFrom":subQ1}),1.0]])]});}
            var Q5;
            {var subQ0=sQuery(id+"F1.wireOp",EDGE,"E234");var subQ1=sQuery(id+"F1.wireOp",EDGE,"3a61cfe4-ae7e-431c-9541-1621a5e99a6d");var subQ2=makeQuery(id+"F1.imprint","INTERSECT",VERTEX,{"derivedFrom":[subQ1,subQ0]});Q5=makeQuery(id+"F1.imprint","IMPRINT",FACE,{"disambiguationData":[TD([[makeQuery(id+"F1.imprint","IMPRINT",EDGE,{"disambiguationData":[TD([[subQ2,-1.0]])],"derivedFrom":subQ1}),-1.0]])]});}
            var Q6;
            {var subQ0=sQuery(id+"F1.wireOp",EDGE,"E234");var subQ1=sQuery(id+"F1.wireOp",EDGE,"435c0a83-62e8-43be-807a-781dea070604");var subQ2=makeQuery(id+"F1.imprint","INTERSECT",VERTEX,{"derivedFrom":[subQ1,subQ0]});Q6=makeQuery(id+"F1.imprint","IMPRINT",FACE,{"disambiguationData":[TD([[makeQuery(id+"F1.imprint","IMPRINT",EDGE,{"disambiguationData":[TD([[subQ2,-1.0]])],"derivedFrom":subQ1}),1.0]])]});}
            var Q7;
            Q7=makeQuery(id+"F1.imprint","IMPRINT",FACE,{"disambiguationData":[TD([[makeQuery(id+"F1.imprint","IMPRINT",EDGE,{"derivedFrom":sQuery(id+"F1.wireOp",EDGE,"E235")}),-1.0]])]});
            var Q8;
            {var subQ1=sQuery(id+"F1.wireOp",EDGE,"53d5dcf0-674b-4c79-9443-bd6d82ffb135");var subQ3=sQuery(id+"F1.wireOp",EDGE,"E244");var subQ4=makeQuery(id+"F1.imprint","INTERSECT",VERTEX,{"derivedFrom":[subQ1,subQ3]});Q8=makeQuery(id+"F1.imprint","IMPRINT",FACE,{"disambiguationData":[TD([[makeQuery(id+"F1.imprint","IMPRINT",EDGE,{"disambiguationData":[TD([[subQ4,-1.0]])],"derivedFrom":subQ3}),1.0]])]});}
            var Q9;
            {var subQ1=sQuery(id+"F1.wireOp",EDGE,"428ab077-734c-40e8-b26b-1190416dde84");var subQ3=sQuery(id+"F1.wireOp",EDGE,"E244");var subQ4=makeQuery(id+"F1.imprint","INTERSECT",VERTEX,{"derivedFrom":[subQ1,subQ3]});Q9=makeQuery(id+"F1.imprint","IMPRINT",FACE,{"disambiguationData":[TD([[makeQuery(id+"F1.imprint","IMPRINT",EDGE,{"disambiguationData":[TD([[subQ4,-1.0]])],"derivedFrom":subQ3}),1.0]])]});}
            var Q10;
            {var subQ1=sQuery(id+"F1.wireOp",EDGE,"428ab077-734c-40e8-b26b-1190416dde84");var subQ3=sQuery(id+"F1.wireOp",EDGE,"E244");var subQ4=makeQuery(id+"F1.imprint","INTERSECT",VERTEX,{"derivedFrom":[subQ1,subQ3]});Q10=makeQuery(id+"F1.imprint","IMPRINT",FACE,{"disambiguationData":[TD([[makeQuery(id+"F1.imprint","IMPRINT",EDGE,{"disambiguationData":[TD([[subQ4,1.0]])],"derivedFrom":subQ3}),1.0]])]});}
            var Q11;
            {var subQ1=sQuery(id+"F1.wireOp",EDGE,"13bed4bd-fcb1-4a5b-8c34-b9fa7a4d6081");var subQ3=sQuery(id+"F1.wireOp",EDGE,"E245");var subQ4=makeQuery(id+"F1.imprint","INTERSECT",VERTEX,{"derivedFrom":[subQ1,subQ3]});Q11=makeQuery(id+"F1.imprint","IMPRINT",FACE,{"disambiguationData":[TD([[makeQuery(id+"F1.imprint","IMPRINT",EDGE,{"disambiguationData":[TD([[subQ4,-1.0]])],"derivedFrom":subQ3}),1.0]])]});}
            var Q12;
            {var subQ1=sQuery(id+"F1.wireOp",EDGE,"13bed4bd-fcb1-4a5b-8c34-b9fa7a4d6081");var subQ3=sQuery(id+"F1.wireOp",EDGE,"E245");var subQ4=makeQuery(id+"F1.imprint","INTERSECT",VERTEX,{"derivedFrom":[subQ1,subQ3]});Q12=makeQuery(id+"F1.imprint","IMPRINT",FACE,{"disambiguationData":[TD([[makeQuery(id+"F1.imprint","IMPRINT",EDGE,{"disambiguationData":[TD([[subQ4,1.0]])],"derivedFrom":subQ3}),1.0]])]});}
            var Q13;
            {var subQ1=sQuery(id+"F1.wireOp",EDGE,"bc46082b-a8de-4a31-b2da-f92bdda07d0f");var subQ3=sQuery(id+"F1.wireOp",EDGE,"E245");var subQ4=makeQuery(id+"F1.imprint","INTERSECT",VERTEX,{"derivedFrom":[subQ1,subQ3]});Q13=makeQuery(id+"F1.imprint","IMPRINT",FACE,{"disambiguationData":[TD([[makeQuery(id+"F1.imprint","IMPRINT",EDGE,{"disambiguationData":[TD([[subQ4,-1.0]])],"derivedFrom":subQ3}),1.0]])]});}
            var Q14;
            {var subQ1=sQuery(id+"F1.wireOp",EDGE,"428ab077-734c-40e8-b26b-1190416dde84");var subQ3=sQuery(id+"F1.wireOp",EDGE,"E245");var subQ4=makeQuery(id+"F1.imprint","INTERSECT",VERTEX,{"derivedFrom":[subQ1,subQ3]});Q14=makeQuery(id+"F1.imprint","IMPRINT",FACE,{"disambiguationData":[TD([[makeQuery(id+"F1.imprint","IMPRINT",EDGE,{"disambiguationData":[TD([[subQ4,-1.0]])],"derivedFrom":subQ3}),1.0]])]});}
            var Q15;
            Q15=makeQuery(id+"F1.imprint","IMPRINT",FACE,{"disambiguationData":[TD([[makeQuery(id+"F1.imprint","IMPRINT",EDGE,{"derivedFrom":sQuery(id+"F1.wireOp",EDGE,"E246")}),1.0]])]});
            var Q16;
            Q16=makeQuery(id+"F1.imprint","IMPRINT",FACE,{"disambiguationData":[TD([[makeQuery(id+"F1.imprint","IMPRINT",EDGE,{"derivedFrom":sQuery(id+"F1.wireOp",EDGE,"E228")}),1.0]])]});
            var Q17;
            Q17=makeQuery(id+"F1.imprint","IMPRINT",FACE,{"disambiguationData":[TD([[makeQuery(id+"F1.imprint","IMPRINT",EDGE,{"derivedFrom":sQuery(id+"F1.wireOp",EDGE,"E227")}),1.0]])]});
            var Q18;
            Q18=makeQuery(id+"F1.imprint","IMPRINT",FACE,{"disambiguationData":[TD([[makeQuery(id+"F1.imprint","IMPRINT",EDGE,{"derivedFrom":sQuery(id+"F1.wireOp",EDGE,"E245")}),1.0]])]});
            var Q19;
            Q19=makeQuery(id+"F1.imprint","IMPRINT",FACE,{"disambiguationData":[TD([[makeQuery(id+"F1.imprint","IMPRINT",EDGE,{"derivedFrom":sQuery(id+"F1.wireOp",EDGE,"E244")}),1.0]])]});
            extrude(context, id + "F6", {"entities" : qUnion([Q0, Q1, Q2, Q3, Q4, Q5, Q6, Q7, Q8, Q9, Q10, Q11, Q12, Q13, Q14, Q15, Q16, Q17, Q18, Q19]), "depth" : 3.1 * mm, "offsetDistance" : 25 * mm});
        }
        {
            var Q0;
            {var subQ0=sQuery(id+"F1.wireOp",EDGE,"E231");Q0=makeQuery(id+"F1.imprint","IMPRINT",FACE,{"disambiguationData":[TD([[makeQuery(id+"F1.imprint","IMPRINT",EDGE,{"derivedFrom":subQ0}),-1.0]])]});}
            var Q1;
            {var subQ0=sQuery(id+"F1.wireOp",EDGE,"E232.MirrorCS");Q1=makeQuery(id+"F1.imprint","IMPRINT",FACE,{"disambiguationData":[TD([[makeQuery(id+"F1.imprint","IMPRINT",EDGE,{"derivedFrom":subQ0}),1.0]])]});}
            var Q2;
            {var subQ0=sQuery(id+"F1.wireOp",EDGE,"E242");Q2=makeQuery(id+"F1.imprint","IMPRINT",FACE,{"disambiguationData":[TD([[makeQuery(id+"F1.imprint","IMPRINT",EDGE,{"derivedFrom":subQ0}),-1.0]])]});}
            var Q3;
            {var subQ0=sQuery(id+"F1.wireOp",EDGE,"E243.MirrorCS");Q3=makeQuery(id+"F1.imprint","IMPRINT",FACE,{"disambiguationData":[TD([[makeQuery(id+"F1.imprint","IMPRINT",EDGE,{"derivedFrom":subQ0}),1.0]])]});}
            extrude(context, id + "F7", {"entities" : qUnion([Q0, Q1, Q2, Q3]), "depth" : 0.8 * mm, "offsetDistance" : 25 * mm});
        }
    });
